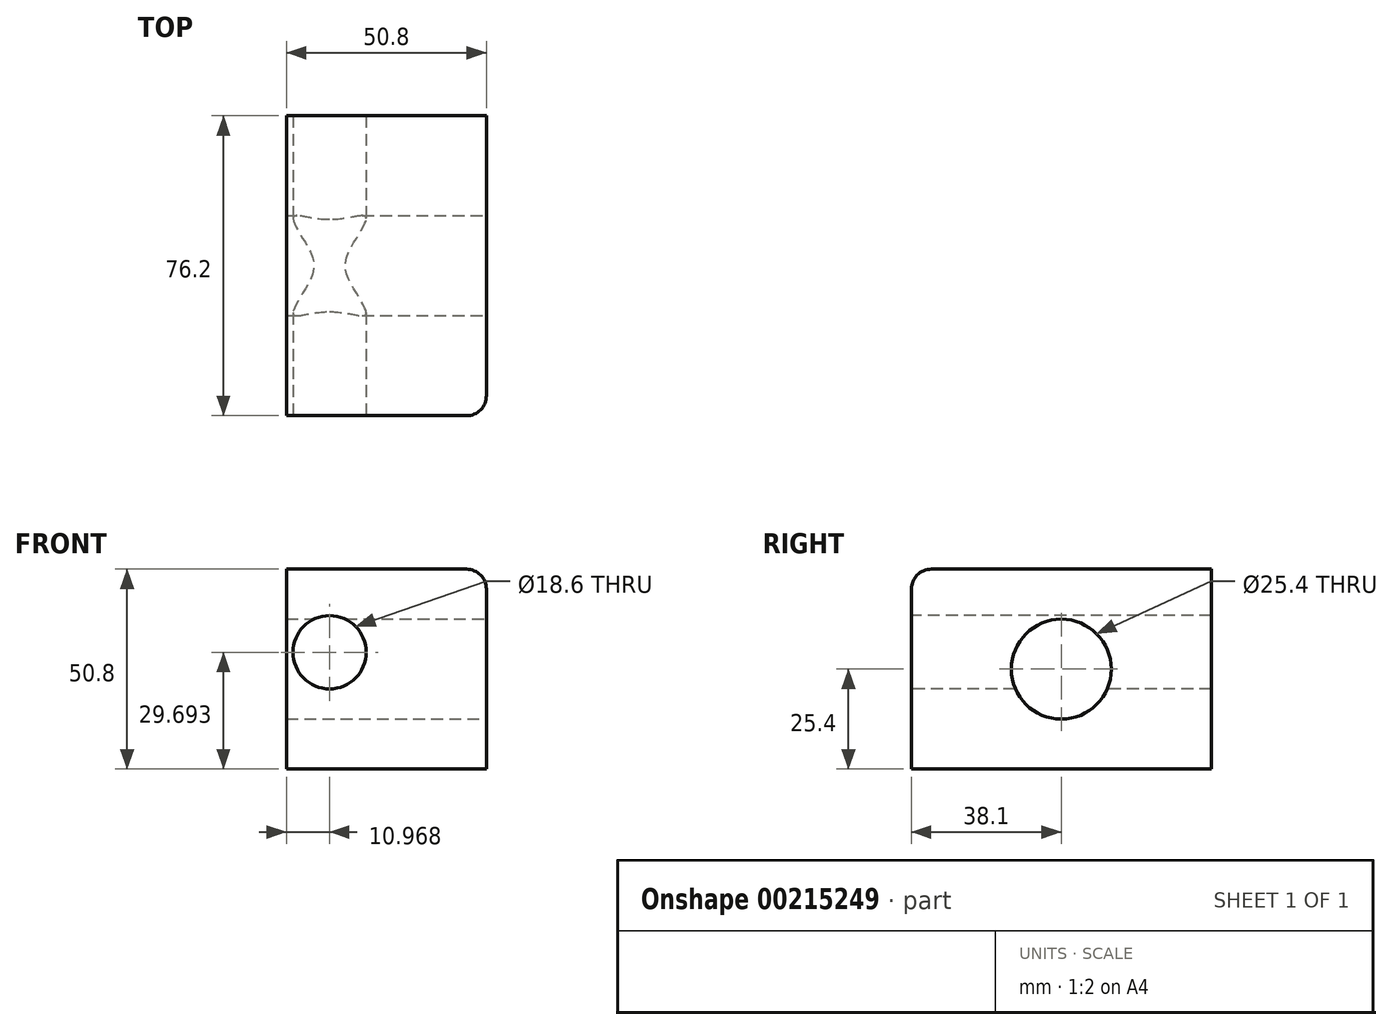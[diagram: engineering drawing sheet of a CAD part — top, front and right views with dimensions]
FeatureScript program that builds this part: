
annotation { "Feature Type Name" : "Feature", "Feature Type Description" : "" }
export const myFeature = defineFeature(function(context is Context, id is Id, definition is map)
    precondition{}
    {
        {
            var Q0;
            Q0=qCreatedBy(makeId("Top.planeOp"),FACE);
            var sketch = newSketch(context, id + "F0", { "sketchPlane" : qUnion([Q0])});
            skLineSegment(sketch, "E0.bottom", {"start": v(-25.4, 38.1) * mm, "end": v(25.4, 38.1) * mm});
            skLineSegment(sketch, "E0.top", {"start": v(-25.4, -38.1) * mm, "end": v(25.4, -38.1) * mm});
            skLineSegment(sketch, "E0.left", {"start": v(-25.4, 38.1) * mm, "end": v(-25.4, -38.1) * mm});
            skLineSegment(sketch, "E0.right", {"start": v(25.4, 38.1) * mm, "end": v(25.4, -38.1) * mm});
            skPoint(sketch, "E0.middle", {"position": v(0, 0) * mm});
            skSolve(sketch);
        }
        {
            var Q0;
            Q0 = qSketchRegion(id + "F0", true);
            extrude(context, id + "F1", {"entities" : qUnion([Q0]), "endBound" : BoundingType.SYMMETRIC, "depth" : 50.8 * mm});
        }
        {
            var Q0;
            Q0=makeQuery(id+"F1.opExtrude","CAP_EDGE",EDGE,{"disambiguationData":[OSD([sQuery(id+"F0.wireOp",EDGE,"E0.right")])],"isStart":false});
            var Q1;
            Q1=makeQuery(id+"F1.opExtrude","SWEPT_EDGE",EDGE,{"disambiguationData":[OSD([sQuery(id+"F0.wireOp",EDGE,"E0.top"),sQuery(id+"F0.wireOp",EDGE,"E0.right")])]});
            var Q2;
            Q2=makeQuery(id+"F1.opExtrude","CAP_EDGE",EDGE,{"disambiguationData":[OSD([sQuery(id+"F0.wireOp",EDGE,"E0.top")])],"isStart":false});
            fillet(context, id + "F2", {"entities" : qUnion([Q0, Q1, Q2]), "radius" : 5.08 * mm, "tangentPropagation" : true, "allowEdgeOverflow" : false});
        }
        {
            var Q0;
            Q0=makeQuery(id+"F1.opExtrude","SWEPT_FACE",FACE,{"disambiguationData":[OSD([sQuery(id+"F0.wireOp",EDGE,"E0.right")])]});
            var sketch = newSketch(context, id + "F3", { "sketchPlane" : qUnion([Q0])});
            skCircle(sketch, "E1", {"center": v(0, 0) * mm, "radius": 12.7 * mm});
            skSolve(sketch);
        }
        {
            var Q0;
            Q0 = qSketchRegion(id + "F3", true);
            extrude(context, id + "F4", {"entities" : qUnion([Q0]), "operationType" : NewBodyOperationType.REMOVE, "endBound" : BoundingType.THROUGH_ALL, "oppositeDirection" : true, "depth" : 25.4 * mm});
        }
        {
            var Q0;
            Q0=makeQuery(id+"F1.opExtrude","SWEPT_FACE",FACE,{"disambiguationData":[OSD([sQuery(id+"F0.wireOp",EDGE,"E0.top")])]});
            var sketch = newSketch(context, id + "F5", { "sketchPlane" : qUnion([Q0])});
            skCircle(sketch, "E2", {"center": v(-14.43, 4.3) * mm, "radius": 9.3 * mm});
            skSolve(sketch);
        }
        {
            var Q0;
            Q0 = qSketchRegion(id + "F5", true);
            extrude(context, id + "F6", {"entities" : qUnion([Q0]), "operationType" : NewBodyOperationType.REMOVE, "endBound" : BoundingType.THROUGH_ALL, "oppositeDirection" : true, "depth" : 25.4 * mm});
        }
    });
